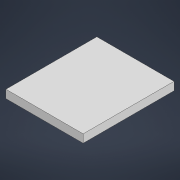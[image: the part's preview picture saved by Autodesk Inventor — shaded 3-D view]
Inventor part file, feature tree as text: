
AUTODESK INVENTOR PART (.ipt)
format: ipt  version: 2022 (Build 260153000, 153)  size: 84,480 bytes
history: native  units: mm
features: other x1, extrude x1, sketch x1
ambient origin geometry x8: Origin, YZ Plane, XZ Plane, XY Plane, X Axis, Y Axis, Z Axis, Center Point
bodies: Body1 (feature_tree)
feature tree (3):
  other  "Твердое тело1"
  extrude  "Выдавливание1"  Depth=209.0mm
  sketch  "Эскиз1"
